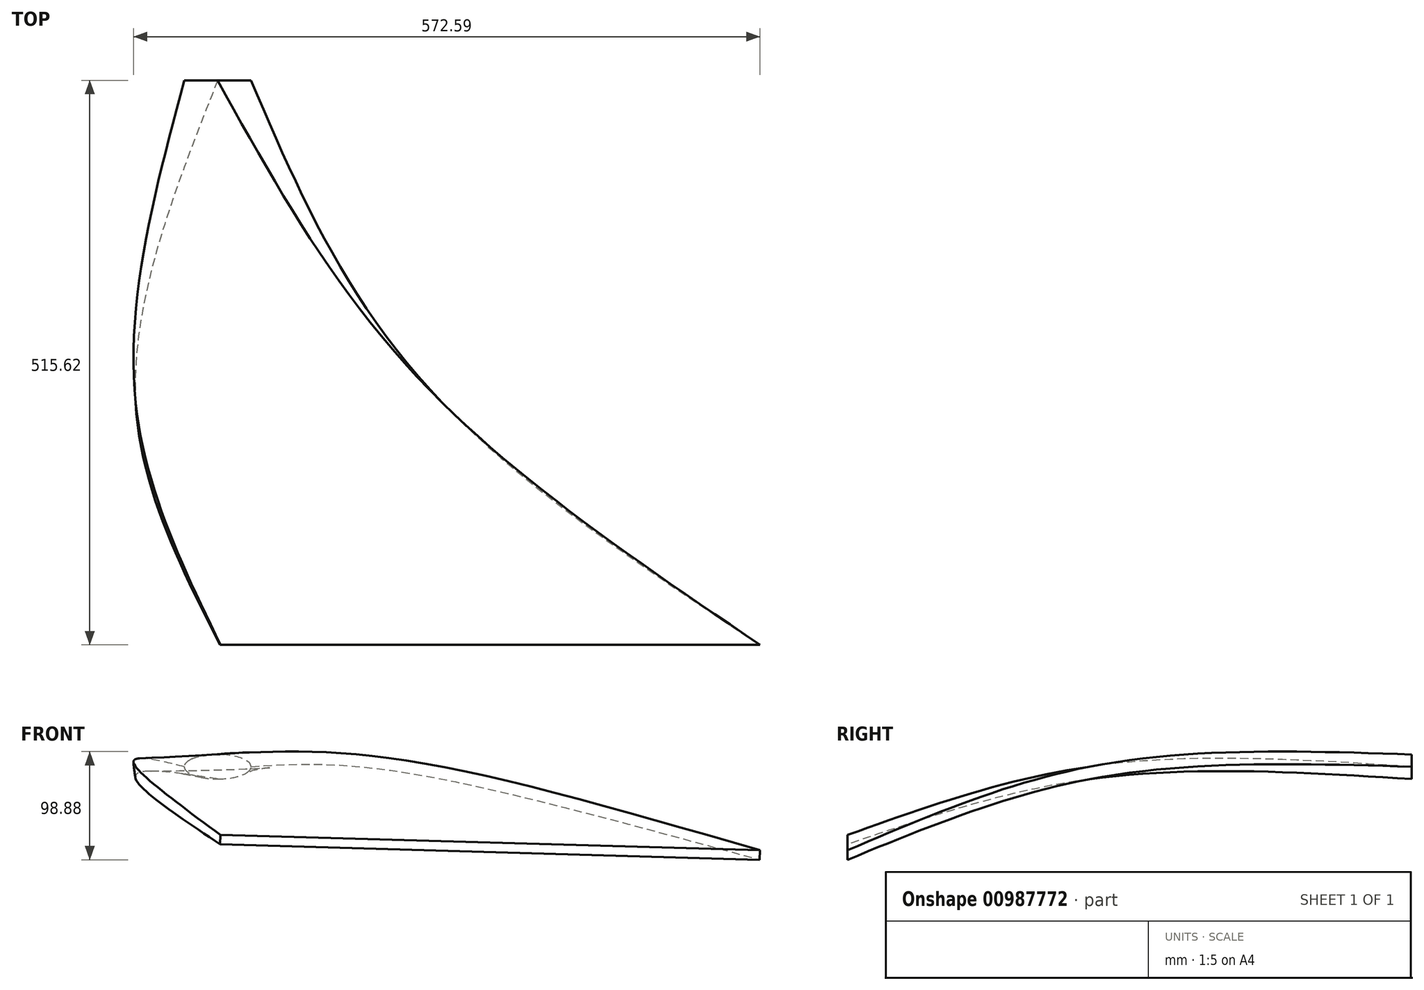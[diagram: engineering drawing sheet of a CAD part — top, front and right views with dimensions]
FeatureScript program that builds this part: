
annotation { "Feature Type Name" : "Feature", "Feature Type Description" : "" }
export const myFeature = defineFeature(function(context is Context, id is Id, definition is map)
    precondition{}
    {
        {
            var Q0;
            Q0=qCreatedBy(makeId("Front.planeOp"),FACE);
            var sketch = newSketch(context, id + "F0", { "sketchPlane" : qUnion([Q0])});
            skEllipse(sketch, "E0", {"center": v(0, 0) * mm, "majorRadius": 30.5 * mm, "minorRadius": 11.18 * mm, "majorAxis": v(-1, 0)});
            skSolve(sketch);
        }
        {
            var Q0;
            Q0=qCreatedBy(makeId("Front.planeOp"),FACE);
            cPlane(context, id + "F1", {"entities" : qUnion([Q0]), "cplaneType" : CPlaneType.OFFSET, "offset" : 294.64 * mm, "width" : 152.4 * mm, "height" : 152.4 * mm});
        }
        {
            var Q0;
            Q0=qCreatedBy(id+"F1.planeOp",FACE);
            var sketch = newSketch(context, id + "F2", { "sketchPlane" : qUnion([Q0])});
            skLineSegment(sketch, "E1.bottom", {"start": v(-74.93, 0) * mm, "end": v(205.45, 0) * mm});
            skLineSegment(sketch, "E1.top", {"start": v(-74.93, -11.4) * mm, "end": v(205.45, -11.4) * mm});
            skLineSegment(sketch, "E1.left", {"start": v(-74.93, 0) * mm, "end": v(-74.93, -11.4) * mm});
            skLineSegment(sketch, "E1.right", {"start": v(205.45, 0) * mm, "end": v(205.45, -11.4) * mm});
            skSolve(sketch);
        }
        {
            var Q0;
            Q0=qCreatedBy(id+"F1.planeOp",FACE);
            cPlane(context, id + "F3", {"entities" : qUnion([Q0]), "cplaneType" : CPlaneType.OFFSET, "offset" : 220.98 * mm, "width" : 152.4 * mm, "height" : 152.4 * mm});
        }
        {
            var Q0;
            Q0=qCreatedBy(id+"F3.planeOp",FACE);
            var sketch = newSketch(context, id + "F4", { "sketchPlane" : qUnion([Q0])});
            skLineSegment(sketch, "E2.bottom", {"start": v(2.3, -70.92) * mm, "end": v(495.4, -85) * mm});
            skLineSegment(sketch, "E2.top", {"start": v(2.54, -62.3) * mm, "end": v(495.64, -76.37) * mm});
            skLineSegment(sketch, "E2.left", {"start": v(2.54, -62.3) * mm, "end": v(2.3, -70.92) * mm});
            skLineSegment(sketch, "E2.right", {"start": v(495.64, -76.37) * mm, "end": v(495.4, -85) * mm});
            skSolve(sketch);
        }
        {
            var Q0;
            Q0=makeQuery(id+"F0.imprint","IMPRINT",FACE,{"disambiguationData":[TD([[makeQuery(id+"F0.imprint","IMPRINT",EDGE,{"derivedFrom":sQuery(id+"F0.wireOp",EDGE,"E0")}),1.0]])]});
            var Q1;
            Q1=makeQuery(id+"F2.imprint","IMPRINT",FACE,{"disambiguationData":[TD([[makeQuery(id+"F2.imprint","IMPRINT",EDGE,{"derivedFrom":sQuery(id+"F2.wireOp",EDGE,"E1.bottom")}),-1.0]])]});
            var Q2;
            Q2=makeQuery(id+"F4.imprint","IMPRINT",FACE,{"disambiguationData":[TD([[makeQuery(id+"F4.imprint","IMPRINT",EDGE,{"derivedFrom":sQuery(id+"F4.wireOp",EDGE,"E2.bottom")}),1.0]])]});
            loft(context, id + "F5", {"sheetProfilesArray" : [{ "sheetProfileEntities" : qUnion([Q0]) }, { "sheetProfileEntities" : qUnion([Q1]) }, { "sheetProfileEntities" : qUnion([Q2]) }]});
        }
    });
